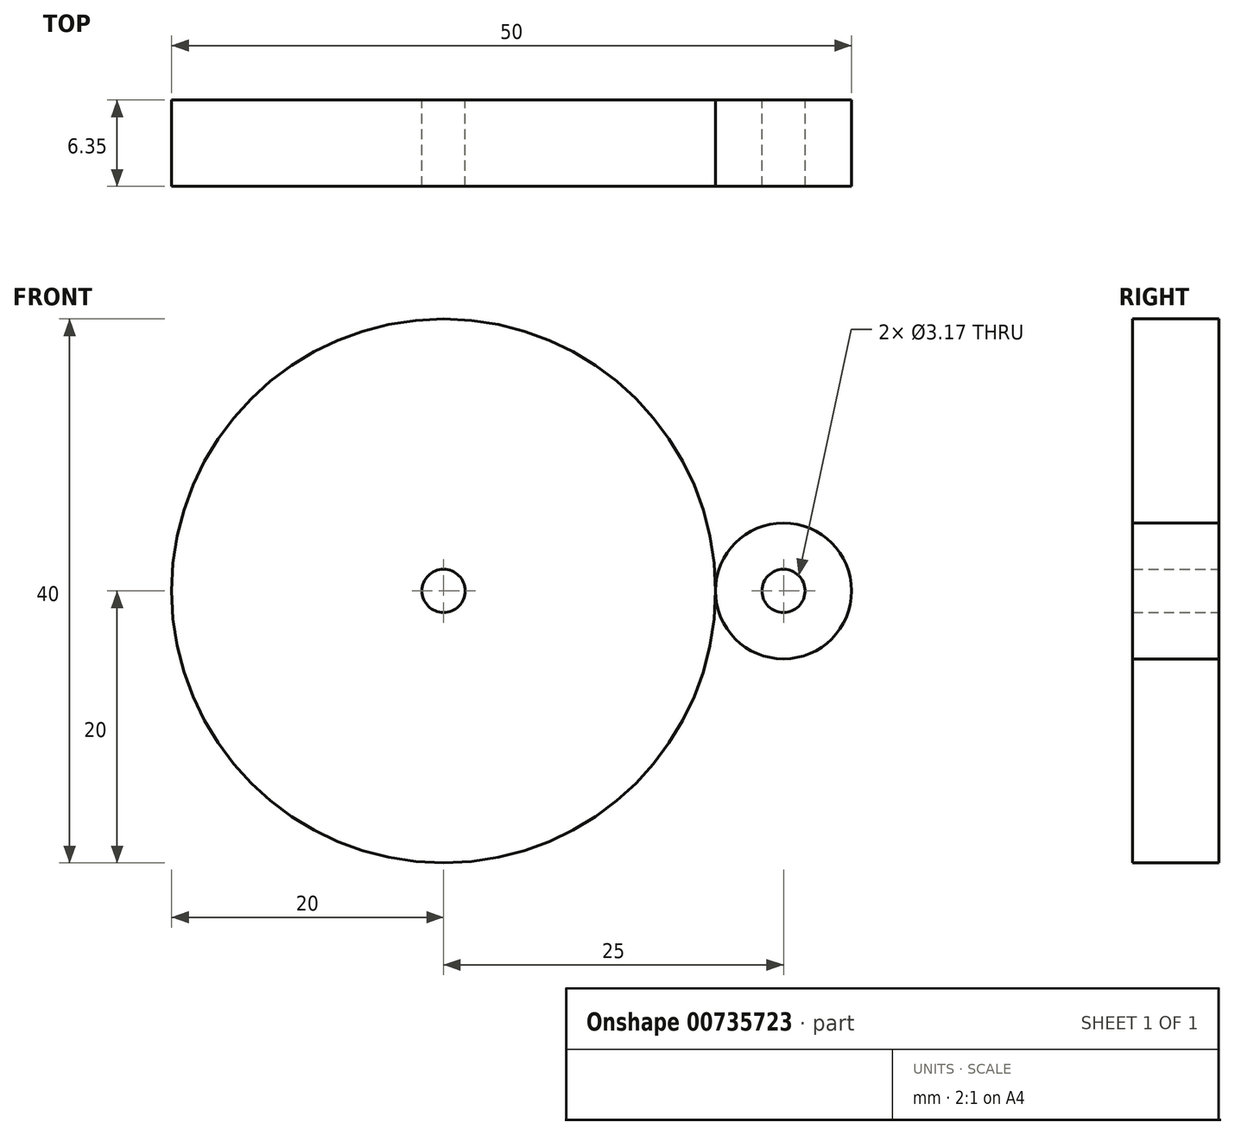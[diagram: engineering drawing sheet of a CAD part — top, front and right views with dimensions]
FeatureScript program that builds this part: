
annotation { "Feature Type Name" : "Feature", "Feature Type Description" : "" }
export const myFeature = defineFeature(function(context is Context, id is Id, definition is map)
    precondition{}
    {
        {
            var Q0;
            Q0=qCreatedBy(makeId("Front.planeOp"),FACE);
            var sketch = newSketch(context, id + "F0", { "sketchPlane" : qUnion([Q0])});
            skCircle(sketch, "E0", {"center": v(0, 0) * mm, "radius": 20 * mm});
            skPoint(sketch, "E1", {"position": v(20, 0) * mm});
            skCircle(sketch, "E2", {"center": v(25, 0) * mm, "radius": 5 * mm});
            skCircle(sketch, "E3", {"center": v(0, 0) * mm, "radius": 1.59 * mm});
            skCircle(sketch, "E4", {"center": v(25, 0) * mm, "radius": 1.59 * mm});
            skSolve(sketch);
        }
        {
            var Q0;
            Q0=makeQuery(id+"F0.imprint","IMPRINT",FACE,{"disambiguationData":[TD([[makeQuery(id+"F0.imprint","IMPRINT",EDGE,{"derivedFrom":sQuery(id+"F0.wireOp",EDGE,"E0")}),1.0]])]});
            var Q1;
            Q1=makeQuery(id+"F0.imprint","IMPRINT",FACE,{"disambiguationData":[TD([[makeQuery(id+"F0.imprint","IMPRINT",EDGE,{"derivedFrom":sQuery(id+"F0.wireOp",EDGE,"E2")}),1.0]])]});
            extrude(context, id + "F1", {"entities" : qUnion([Q0, Q1]), "depth" : 6.35 * mm, "offsetDistance" : 25.4 * mm});
        }
    });
